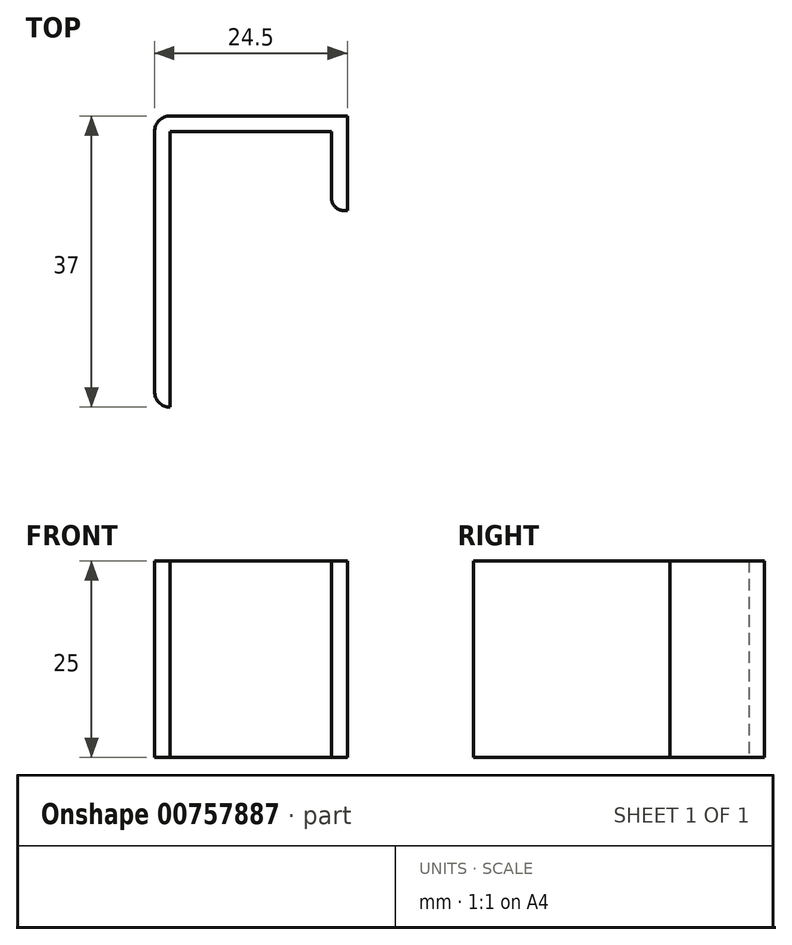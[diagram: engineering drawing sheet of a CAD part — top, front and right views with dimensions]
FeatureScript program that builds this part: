
annotation { "Feature Type Name" : "Feature", "Feature Type Description" : "" }
export const myFeature = defineFeature(function(context is Context, id is Id, definition is map)
    precondition{}
    {
        {
            var Q0;
            Q0=qCreatedBy(makeId("Top.planeOp"),FACE);
            var sketch = newSketch(context, id + "F0", { "sketchPlane" : qUnion([Q0])});
            skLineSegment(sketch, "E0", {"start": v(0, 0) * mm, "end": v(0, -37) * mm});
            skLineSegment(sketch, "E1", {"start": v(0, -37) * mm, "end": v(2, -37) * mm});
            skLineSegment(sketch, "E2", {"start": v(0, 0) * mm, "end": v(24.5, 0) * mm});
            skLineSegment(sketch, "E3", {"start": v(24.5, 0) * mm, "end": v(24.5, -12) * mm});
            skLineSegment(sketch, "E4", {"start": v(24.5, -12) * mm, "end": v(22.5, -12) * mm});
            skLineSegment(sketch, "E5", {"start": v(22.5, -12) * mm, "end": v(22.5, -2) * mm});
            skLineSegment(sketch, "E6", {"start": v(22.5, -2) * mm, "end": v(2, -2) * mm});
            skLineSegment(sketch, "E7", {"start": v(2, -2) * mm, "end": v(2, -37) * mm});
            skSolve(sketch);
        }
        {
            var Q0;
            Q0 = qSketchRegion(id + "F0", true);
            extrude(context, id + "F1", {"entities" : qUnion([Q0]), "depth" : 25 * mm, "offsetDistance" : 25 * mm});
        }
        {
            var Q0;
            Q0=makeQuery(id+"F1.opExtrude","SWEPT_EDGE",EDGE,{"disambiguationData":[OSD([sQuery(id+"F0.wireOp",EDGE,"E4"),sQuery(id+"F0.wireOp",EDGE,"E5")])]});
            fillet(context, id + "F2", {"entities" : qUnion([Q0]), "radius" : 1.5 * mm, "tangentPropagation" : true, "allowEdgeOverflow" : false});
        }
        {
            var Q0;
            Q0=makeQuery(id+"F1.opExtrude","SWEPT_EDGE",EDGE,{"disambiguationData":[OSD([sQuery(id+"F0.wireOp",EDGE,"E0"),sQuery(id+"F0.wireOp",EDGE,"E2")])]});
            var Q1;
            Q1=makeQuery(id+"F1.opExtrude","SWEPT_EDGE",EDGE,{"disambiguationData":[OSD([sQuery(id+"F0.wireOp",EDGE,"E0"),sQuery(id+"F0.wireOp",EDGE,"E1")])]});
            fillet(context, id + "F3", {"entities" : qUnion([Q0, Q1]), "radius" : 2 * mm, "tangentPropagation" : true, "allowEdgeOverflow" : false});
        }
    });
